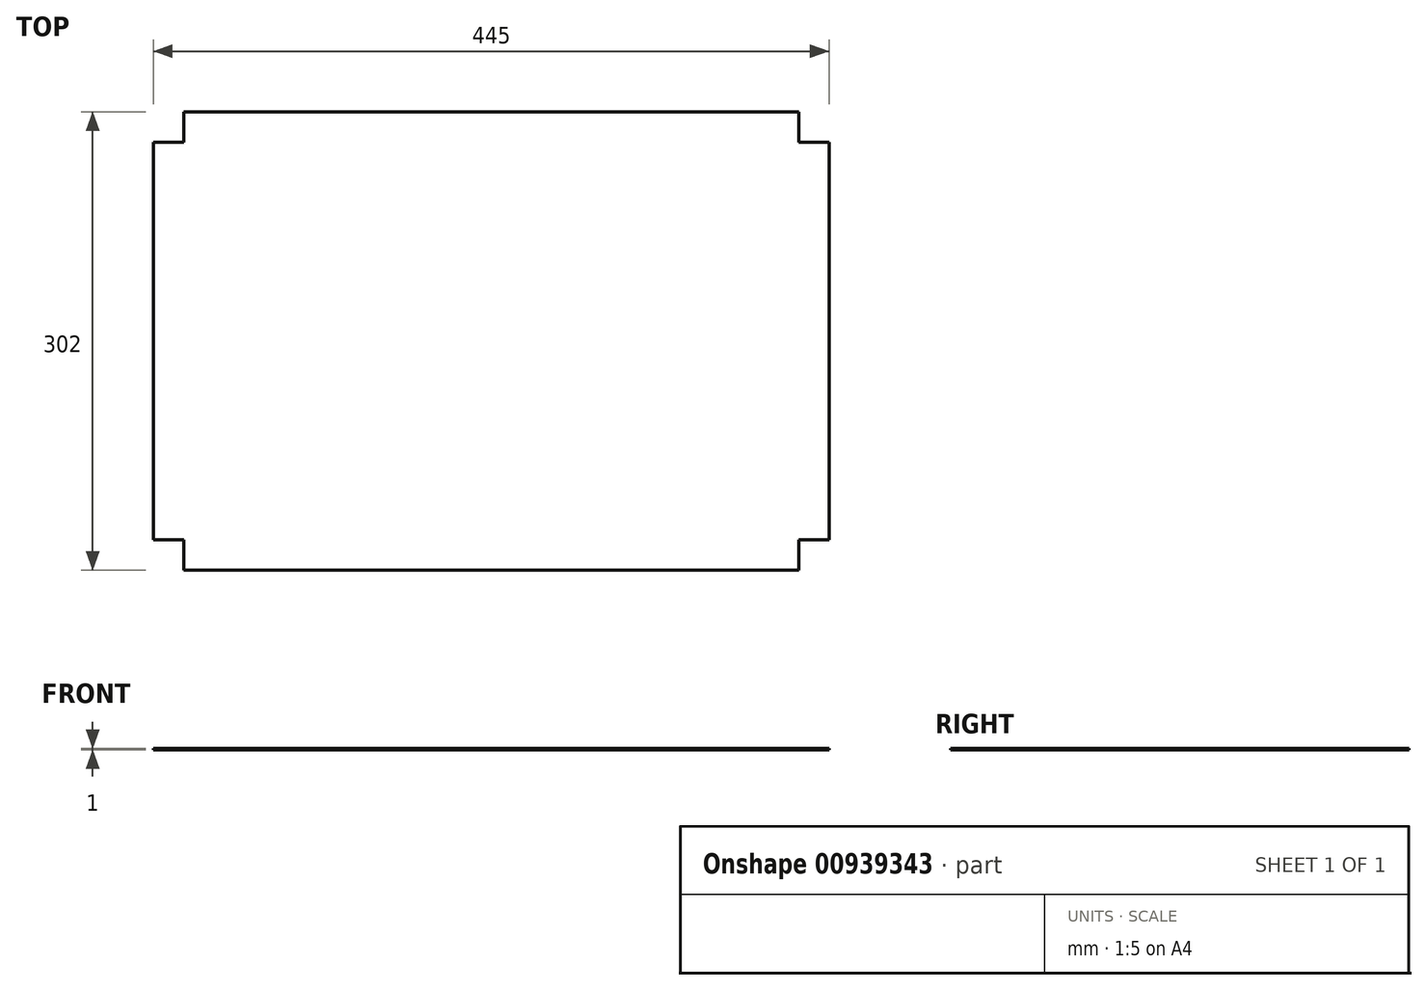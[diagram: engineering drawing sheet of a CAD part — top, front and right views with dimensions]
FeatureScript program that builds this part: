
annotation { "Feature Type Name" : "Feature", "Feature Type Description" : "" }
export const myFeature = defineFeature(function(context is Context, id is Id, definition is map)
    precondition{}
    {
        {
            var Q0;
            Q0=qCreatedBy(makeId("Top.planeOp"),FACE);
            var sketch = newSketch(context, id + "F0", { "sketchPlane" : qUnion([Q0])});
            skLineSegment(sketch, "E0.bottom", {"start": v(202.5, -151) * mm, "end": v(-202.5, -151) * mm});
            skLineSegment(sketch, "E0.top", {"start": v(202.5, 151) * mm, "end": v(-202.5, 151) * mm});
            skLineSegment(sketch, "E0.left", {"start": v(222.5, -131) * mm, "end": v(222.5, 131) * mm});
            skLineSegment(sketch, "E0.right", {"start": v(-222.5, -131) * mm, "end": v(-222.5, 131) * mm});
            skPoint(sketch, "E0.middle", {"position": v(0, 0) * mm});
            skLineSegment(sketch, "E1", {"start": v(-222.5, -131) * mm, "end": v(-202.5, -131) * mm});
            skLineSegment(sketch, "E2", {"start": v(-202.5, -131) * mm, "end": v(-202.5, -151) * mm});
            skLineSegment(sketch, "E3", {"start": v(-222.5, 131) * mm, "end": v(-202.5, 131) * mm});
            skLineSegment(sketch, "E4", {"start": v(-202.5, 131) * mm, "end": v(-202.5, 151) * mm});
            skLineSegment(sketch, "E5", {"start": v(202.5, 151) * mm, "end": v(202.5, 131) * mm});
            skLineSegment(sketch, "E6", {"start": v(202.5, 131) * mm, "end": v(222.5, 131) * mm});
            skLineSegment(sketch, "E7", {"start": v(222.5, -131) * mm, "end": v(202.5, -131) * mm});
            skLineSegment(sketch, "E8", {"start": v(202.5, -131) * mm, "end": v(202.5, -151) * mm});
            skPoint(sketch, "E9.orphan", {"position": v(-222.5, 151) * mm});
            skPoint(sketch, "E10.orphan", {"position": v(222.5, 151) * mm});
            skPoint(sketch, "E11.orphan", {"position": v(-222.5, -151) * mm});
            skPoint(sketch, "E12.orphan", {"position": v(222.5, -151) * mm});
            skSolve(sketch);
        }
        {
            var Q0;
            Q0 = qSketchRegion(id + "F0", true);
            extrude(context, id + "F1", {"entities" : qUnion([Q0]), "depth" : 1 * mm, "offsetDistance" : 25 * mm});
        }
    });
